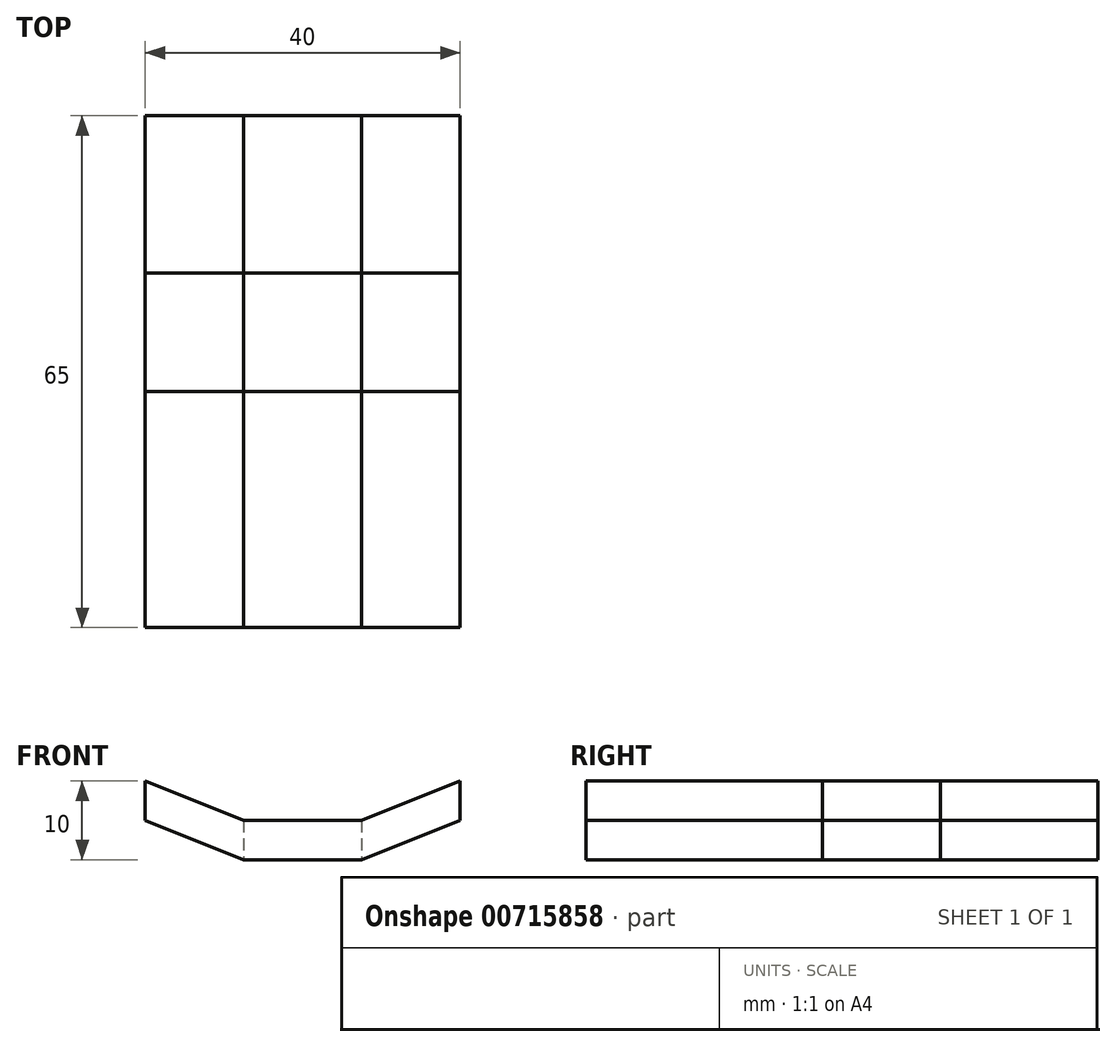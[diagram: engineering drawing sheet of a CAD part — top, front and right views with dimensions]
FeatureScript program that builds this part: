
annotation { "Feature Type Name" : "Feature", "Feature Type Description" : "" }
export const myFeature = defineFeature(function(context is Context, id is Id, definition is map)
    precondition{}
    {
        {
            var Q0;
            Q0=qCreatedBy(makeId("Front.planeOp"),FACE);
            var sketch = newSketch(context, id + "F0", { "sketchPlane" : qUnion([Q0])});
            skLineSegment(sketch, "E0.bottom", {"start": v(-53.47, 5) * mm, "end": v(-38.47, 5) * mm});
            skLineSegment(sketch, "E0.top", {"start": v(-53.47, 0) * mm, "end": v(-38.47, 0) * mm});
            skLineSegment(sketch, "E0.left", {"start": v(-53.47, 5) * mm, "end": v(-53.47, 0) * mm});
            skLineSegment(sketch, "E0.right", {"start": v(-38.47, 5) * mm, "end": v(-38.47, 0) * mm});
            skLineSegment(sketch, "E1", {"start": v(-53.47, 0) * mm, "end": v(-65.97, 5) * mm});
            skLineSegment(sketch, "E2", {"start": v(-65.97, 5) * mm, "end": v(-65.97, 10) * mm});
            skLineSegment(sketch, "E3", {"start": v(-65.97, 10) * mm, "end": v(-53.47, 5) * mm});
            skLineSegment(sketch, "E4", {"start": v(-38.47, 5) * mm, "end": v(-25.97, 10) * mm});
            skLineSegment(sketch, "E5", {"start": v(-25.97, 10) * mm, "end": v(-25.97, 5) * mm});
            skLineSegment(sketch, "E6", {"start": v(-25.97, 5) * mm, "end": v(-38.47, 0) * mm});
            skSolve(sketch);
        }
        {
            var Q0;
            Q0 = qSketchRegion(id + "F0", true);
            extrude(context, id + "F1", {"entities" : qUnion([Q0]), "depth" : 30 * mm, "offsetDistance" : 25 * mm});
        }
        {
            var Q0;
            Q0=makeQuery(id+"F0.imprint","IMPRINT",FACE,{"disambiguationData":[TD([[makeQuery(id+"F0.imprint","IMPRINT",EDGE,{"derivedFrom":sQuery(id+"F0.wireOp",EDGE,"E0.right")}),1.0]])]});
            var Q1;
            Q1=makeQuery(id+"F0.imprint","IMPRINT",FACE,{"disambiguationData":[TD([[makeQuery(id+"F0.imprint","IMPRINT",EDGE,{"derivedFrom":sQuery(id+"F0.wireOp",EDGE,"E0.left")}),-1.0]])]});
            extrude(context, id + "F2", {"entities" : qUnion([Q0, Q1]), "oppositeDirection" : true, "depth" : 15 * mm, "offsetDistance" : 25 * mm});
        }
        {
            var Q0;
            Q0=makeQuery(id+"F2.opExtrude","CAP_FACE",FACE,{"disambiguationData":[OSD([sQuery(id+"F0.wireOp",EDGE,"E0.right"),sQuery(id+"F0.wireOp",EDGE,"E4"),sQuery(id+"F0.wireOp",EDGE,"E5"),sQuery(id+"F0.wireOp",EDGE,"E6")])],"isStart":false});
            var Q1;
            Q1=makeQuery(id+"F2.opExtrude","CAP_FACE",FACE,{"disambiguationData":[OSD([sQuery(id+"F0.wireOp",EDGE,"E0.left"),sQuery(id+"F0.wireOp",EDGE,"E1"),sQuery(id+"F0.wireOp",EDGE,"E2"),sQuery(id+"F0.wireOp",EDGE,"E3")])],"isStart":false});
            extrude(context, id + "F3", {"entities" : qUnion([Q0, Q1]), "depth" : 20 * mm, "offsetDistance" : 25 * mm});
        }
        {
            var Q0;
            Q0=makeQuery(id+"F3.opExtrude","SWEPT_FACE",FACE,{"disambiguationData":[OSD([sQuery(id+"F0.wireOp",EDGE,"E0.right")])]});
            extrude(context, id + "F4", {"entities" : qUnion([Q0]), "depth" : 15 * mm, "offsetDistance" : 25 * mm});
        }
    });
